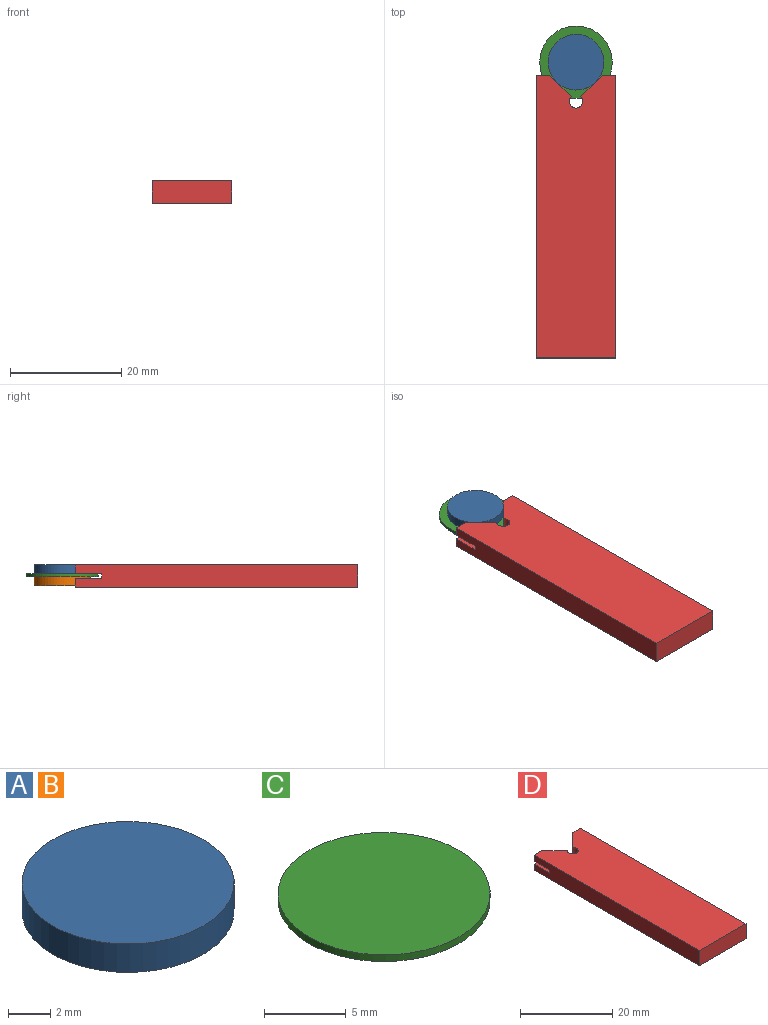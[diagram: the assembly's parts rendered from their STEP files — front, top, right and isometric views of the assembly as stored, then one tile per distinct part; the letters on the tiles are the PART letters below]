
ASSEMBLY  parts=4 mates=3
PART A: 3 faces, bbox 10x10x1.6 mm
  f0: cylinder r=5mm len=10mm, axis (0,0,-1), area 51.5mm2, adj f1,f2
  f1: plane 10x10mm, normal (0,0,1), area 78.5mm2, adj f0
  f2: plane 10x10mm, normal (0,0,-1), area 78.5mm2, adj f0
PART B: same geometry as A
PART C: 3 faces, bbox 13x13x0.5 mm
  f0: cylinder r=6.5mm len=13mm, axis (0,0,-1), area 20.4mm2, adj f1,f2
  f1: plane 13x13mm, normal (0,0,1), area 132.7mm2, adj f0
  f2: plane 13x13mm, normal (0,0,-1), area 132.7mm2, adj f0
PART D: 20 faces, bbox 14.3x50.8x4 mm
  f0: plane 2.38x1.6mm, normal (0,1,0), area 3.8mm2, adj f6,f8,f13,f17
  f1: plane 2.38x1.6mm, normal (0,1,0), area 3.8mm2, adj f3,f11,f13,f14
  f2: plane 3.92x3.92mm, normal (0.71,0.71,0), area 8.9mm2, adj f5,f7,f12,f18
  f3: plane 50.8x4mm, normal (1,0,0), area 199.4mm2, adj f1,f9,f10,f12,f13,f14,f15,f16
  f4: plane 3.92x3.92mm, normal (-0.71,0.71,0), area 8.9mm2, adj f5,f10,f12,f15
  f5: cylinder r=1.19mm len=4mm, axis (0,0,-1), area 20.9mm2, adj f2,f4,f6,f11,f12,f13,f14,f15
  f6: plane 3.92x3.92mm, normal (0.71,0.71,0), area 8.9mm2, adj f0,f5,f13,f17
  f7: plane 2.38x1.6mm, normal (0,1,0), area 3.8mm2, adj f2,f8,f12,f18
  f8: plane 50.8x4mm, normal (-1,0,0), area 199.4mm2, adj f0,f7,f9,f12,f13,f17,f18,f19
  f9: plane 14.29x4mm, normal (0,-1,0), area 57.1mm2, adj f3,f8,f12,f13
  f10: plane 2.38x1.6mm, normal (0,1,0), area 3.8mm2, adj f3,f4,f12,f15
  f11: plane 3.92x3.92mm, normal (-0.71,0.71,0), area 8.9mm2, adj f1,f5,f13,f14
  f12: plane 50.8x14.29mm, normal (0,0,1), area 699.8mm2, adj f2,f3,f4,f5,f7,f8,f9,f10
  f13: plane 50.8x14.29mm, normal (0,0,-1), area 699.8mm2, adj f0,f1,f3,f5,f6,f8,f9,f11
  f14: plane 6.3x4.76mm, normal (0,0,1), area 22.1mm2, adj f1,f3,f5,f11,f16
  f15: plane 6.3x4.76mm, normal (0,0,-1), area 22.1mm2, adj f3,f4,f5,f10,f16
  f16: plane 5.95x0.8mm, normal (0,1,0), area 4.8mm2, adj f3,f5,f14,f15
  f17: plane 6.3x4.76mm, normal (0,0,1), area 22.1mm2, adj f0,f5,f6,f8,f19
  f18: plane 6.3x4.76mm, normal (0,0,-1), area 22.1mm2, adj f2,f5,f7,f8,f19
  f19: plane 5.95x0.8mm, normal (0,1,0), area 4.8mm2, adj f5,f8,f17,f18
PLACE A rot(axis=(1,0,0),180deg) t=(0,28.58,0)mm
PLACE B rot(axis=(1,0,0),180deg) t=(0,28.58,-2.14)mm
PLACE C rot(axis=(1,0,0),180deg) t=(0,28.58,-1.64)mm
PLACE D t=(0,0.87,-4)mm
MATE fastened C.f0 <-> A.f0  axis (0,0,1) through (0,28.58,-1.64)mm
MATE planar A.f0 <-> D.f12  axis (0,0,1) through (0,28.58,0)mm
MATE fastened B.f0 <-> C.f0  axis (0,0,1) through (0,28.58,-2.14)mm
